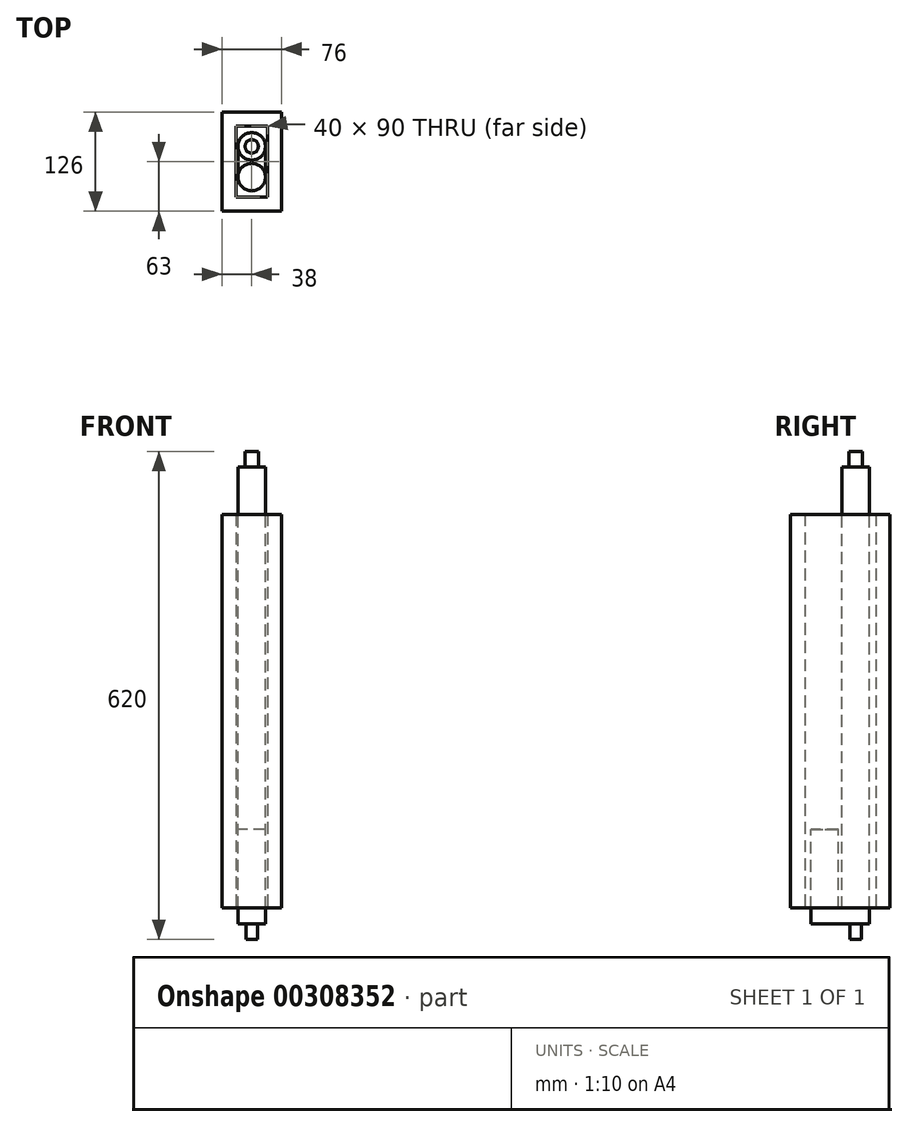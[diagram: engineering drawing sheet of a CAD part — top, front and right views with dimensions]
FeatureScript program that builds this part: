
annotation { "Feature Type Name" : "Feature", "Feature Type Description" : "" }
export const myFeature = defineFeature(function(context is Context, id is Id, definition is map)
    precondition{}
    {
        {
            var Q0;
            Q0=qCreatedBy(makeId("Top.planeOp"),FACE);
            var sketch = newSketch(context, id + "F0", { "sketchPlane" : qUnion([Q0])});
            skLineSegment(sketch, "E0.bottom", {"start": v(20, -45) * mm, "end": v(-20, -45) * mm});
            skLineSegment(sketch, "E0.top", {"start": v(20, 45) * mm, "end": v(-20, 45) * mm});
            skLineSegment(sketch, "E0.left", {"start": v(20, -45) * mm, "end": v(20, 45) * mm});
            skLineSegment(sketch, "E0.right", {"start": v(-20, -45) * mm, "end": v(-20, 45) * mm});
            skPoint(sketch, "E0.middle", {"position": v(0, 0) * mm});
            skLineSegment(sketch, "E1.0", {"start": v(38, -63) * mm, "end": v(38, 63) * mm});
            skLineSegment(sketch, "E1.1", {"start": v(38, -63) * mm, "end": v(-38, -63) * mm});
            skLineSegment(sketch, "E1.2", {"start": v(-38, -63) * mm, "end": v(-38, 63) * mm});
            skLineSegment(sketch, "E1.3", {"start": v(38, 63) * mm, "end": v(-38, 63) * mm});
            skSolve(sketch);
        }
        {
            var Q0;
            Q0=qCreatedBy(makeId("Top.planeOp"),FACE);
            var sketch = newSketch(context, id + "F1", { "sketchPlane" : qUnion([Q0])});
            skCircle(sketch, "E2", {"center": v(0, -19.5) * mm, "radius": 17.5 * mm});
            skCircle(sketch, "E3", {"center": v(0, 19.5) * mm, "radius": 17.5 * mm});
            skLineSegment(sketch, "E4", {"start": v(-17.5, -19.5) * mm, "end": v(-17.5, 19.5) * mm});
            skLineSegment(sketch, "E5", {"start": v(17.5, 19.5) * mm, "end": v(17.5, -19.5) * mm});
            skLineSegment(sketch, "E6.bottom", {"start": v(-7.5, 12) * mm, "end": v(7.5, 12) * mm});
            skLineSegment(sketch, "E6.top", {"start": v(-7.5, 27) * mm, "end": v(7.5, 27) * mm});
            skLineSegment(sketch, "E6.left", {"start": v(-7.5, 12) * mm, "end": v(-7.5, 27) * mm});
            skLineSegment(sketch, "E6.right", {"start": v(7.5, 12) * mm, "end": v(7.5, 27) * mm});
            skSolve(sketch);
        }
        {
            var Q0;
            {var subQ0=sQuery(id+"F1.wireOp",EDGE,"E4");Q0=makeQuery(id+"F1.imprint","IMPRINT",FACE,{"disambiguationData":[TD([[makeQuery(id+"F1.imprint","IMPRINT",EDGE,{"derivedFrom":subQ0}),-1.0]])]});}
            var Q1;
            {var subQ0=sQuery(id+"F1.wireOp",EDGE,"E3");var subQ1=makeQuery(id+"F1.imprint","INTERSECT",VERTEX,{"derivedFrom":[subQ0,sQuery(id+"F1.wireOp",EDGE,"E4")]});Q1=makeQuery(id+"F1.imprint","IMPRINT",FACE,{"disambiguationData":[TD([[makeQuery(id+"F1.imprint","IMPRINT",EDGE,{"disambiguationData":[TD([[subQ1,1.0]])],"derivedFrom":subQ0}),1.0]])]});}
            var Q2;
            {var subQ0=sQuery(id+"F1.wireOp",EDGE,"E2");var subQ1=makeQuery(id+"F1.imprint","INTERSECT",VERTEX,{"derivedFrom":[subQ0,sQuery(id+"F1.wireOp",EDGE,"E4")]});Q2=makeQuery(id+"F1.imprint","IMPRINT",FACE,{"disambiguationData":[TD([[makeQuery(id+"F1.imprint","IMPRINT",EDGE,{"disambiguationData":[TD([[subQ1,1.0]])],"derivedFrom":subQ0}),1.0]])]});}
            var Q3;
            Q3=makeQuery(id+"F1.imprint","IMPRINT",FACE,{"disambiguationData":[TD([[makeQuery(id+"F1.imprint","IMPRINT",EDGE,{"derivedFrom":sQuery(id+"F1.wireOp",EDGE,"E6.bottom")}),1.0]])]});
            extrude(context, id + "F2", {"entities" : qUnion([Q0, Q1, Q2, Q3]), "oppositeDirection" : true, "depth" : 20 * mm});
        }
        {
            var Q0;
            {var subQ0=sQuery(id+"F1.wireOp",EDGE,"E2");var subQ1=makeQuery(id+"F1.imprint","INTERSECT",VERTEX,{"derivedFrom":[subQ0,sQuery(id+"F1.wireOp",EDGE,"E4")]});Q0=makeQuery(id+"F1.imprint","IMPRINT",FACE,{"disambiguationData":[TD([[makeQuery(id+"F1.imprint","IMPRINT",EDGE,{"disambiguationData":[TD([[subQ1,1.0]])],"derivedFrom":subQ0}),1.0]])]});}
            extrude(context, id + "F3", {"entities" : qUnion([Q0]), "operationType" : NewBodyOperationType.ADD, "depth" : 100 * mm});
        }
        {
            var Q0;
            {var subQ0=sQuery(id+"F1.wireOp",EDGE,"E3");var subQ1=makeQuery(id+"F1.imprint","INTERSECT",VERTEX,{"derivedFrom":[subQ0,sQuery(id+"F1.wireOp",EDGE,"E4")]});Q0=makeQuery(id+"F1.imprint","IMPRINT",FACE,{"disambiguationData":[TD([[makeQuery(id+"F1.imprint","IMPRINT",EDGE,{"disambiguationData":[TD([[subQ1,1.0]])],"derivedFrom":subQ0}),1.0]])]});}
            var Q1;
            Q1=makeQuery(id+"F1.imprint","IMPRINT",FACE,{"disambiguationData":[TD([[makeQuery(id+"F1.imprint","IMPRINT",EDGE,{"derivedFrom":sQuery(id+"F1.wireOp",EDGE,"E6.bottom")}),1.0]])]});
            extrude(context, id + "F4", {"entities" : qUnion([Q0, Q1]), "operationType" : NewBodyOperationType.ADD, "depth" : 560 * mm});
        }
        {
            var Q0;
            Q0=makeQuery(id+"F1.imprint","IMPRINT",FACE,{"disambiguationData":[TD([[makeQuery(id+"F1.imprint","IMPRINT",EDGE,{"derivedFrom":sQuery(id+"F1.wireOp",EDGE,"E6.bottom")}),1.0]])]});
            extrude(context, id + "F5", {"entities" : qUnion([Q0]), "operationType" : NewBodyOperationType.ADD, "oppositeDirection" : true, "depth" : 40 * mm});
        }
        {
            var Q0;
            Q0=makeQuery(id+"F4.opExtrude","CAP_FACE",FACE,{"disambiguationData":[OSD([sQuery(id+"F1.wireOp",EDGE,"E3")])],"isStart":false});
            var sketch = newSketch(context, id + "F6", { "sketchPlane" : qUnion([Q0])});
            skCircle(sketch, "E7", {"center": v(0, 19.5) * mm, "radius": 8.5 * mm});
            skSolve(sketch);
        }
        {
            var Q0;
            Q0=makeQuery(id+"F6.imprint","IMPRINT",FACE,{"disambiguationData":[TD([[makeQuery(id+"F6.imprint","IMPRINT",EDGE,{"derivedFrom":sQuery(id+"F6.wireOp",EDGE,"E7")}),1.0]])]});
            extrude(context, id + "F7", {"entities" : qUnion([Q0]), "operationType" : NewBodyOperationType.ADD, "depth" : 20 * mm});
        }
        {
            var Q0;
            Q0=makeQuery(id+"F0.imprint","IMPRINT",FACE,{"disambiguationData":[TD([[makeQuery(id+"F0.imprint","IMPRINT",EDGE,{"derivedFrom":sQuery(id+"F0.wireOp",EDGE,"E0.bottom")}),1.0]])]});
            extrude(context, id + "F8", {"entities" : qUnion([Q0]), "depth" : 500 * mm});
        }
    });
